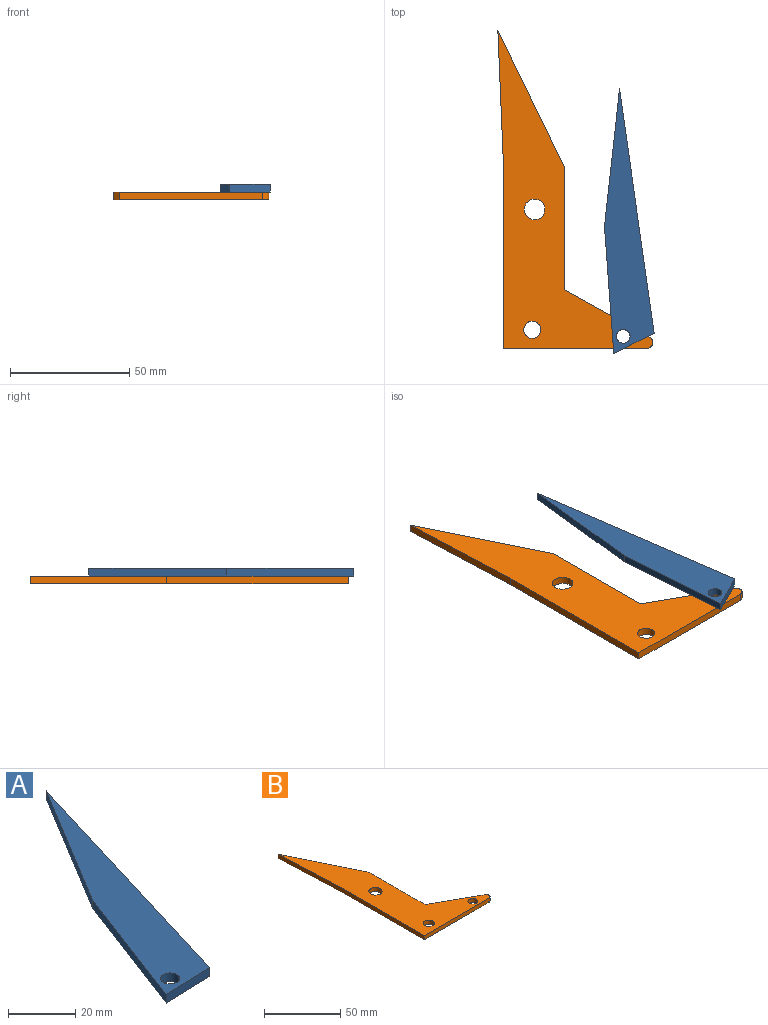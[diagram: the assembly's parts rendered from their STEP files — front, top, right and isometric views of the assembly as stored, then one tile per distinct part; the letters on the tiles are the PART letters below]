
ASSEMBLY  parts=2 mates=1
PART A: 7 faces, bbox 49.1x99.5x3.2 mm
  f0: plane 49.68x30.14mm, normal (-0.85,0.52,0), area 184.5mm2, adj f1,f3,f5,f6
  f1: plane 49.87x18.95mm, normal (-0.93,0.36,0), area 169.4mm2, adj f0,f2,f5,f6
  f2: plane 18.95x3.18mm, normal (0.03,-1,0), area 60.2mm2, adj f1,f3,f5,f6
  f3: plane 98.96x30.14mm, normal (0.96,-0.29,0), area 328.4mm2, adj f0,f2,f5,f6
  f4: cylinder r=2.86mm len=5.72mm, axis (0,0,-1), area 57mm2, adj f5,f6
  f5: plane 99.55x49.09mm, normal (0,0,1), area 1183.9mm2, adj f0,f1,f2,f3,f4
  f6: plane 99.55x49.09mm, normal (0,0,-1), area 1183.9mm2, adj f0,f1,f2,f3,f4
PART B: 12 faces, bbox 64.9x133.3x3.2 mm
  f0: plane 57.1x3.18mm, normal (-1,-0.04,0), area 181.5mm2, adj f1,f8,f10,f11
  f1: plane 76.2x3.18mm, normal (-1,0,0), area 241.9mm2, adj f0,f2,f10,f11
  f2: plane 60.01x3.18mm, normal (0,-1,0), area 190.5mm2, adj f1,f3,f10,f11
  f3: cylinder r=2.54mm len=4.76mm, axis (0,0,-1), area 21.3mm2, adj f2,f4,f10,f11
  f4: plane 35.84x19.83mm, normal (0.48,0.88,0), area 130.1mm2, adj f3,f5,f10,f11
  f5: plane 51.61x3.18mm, normal (1,0,0), area 163.9mm2, adj f4,f8,f10,f11
  f6: cylinder r=3.61mm len=7.21mm, axis (0,0,-1), area 71.9mm2, adj f10,f11
  f7: cylinder r=3.17mm len=6.35mm, axis (0,0,-1), area 63.3mm2, adj f10,f11
  f8: plane 57.1x27.78mm, normal (0.9,0.44,0), area 201.6mm2, adj f0,f5,f10,f11
  f9: cylinder r=4.33mm len=8.66mm, axis (0,0,-1), area 86.3mm2, adj f10,f11
  f10: plane 133.3x64.93mm, normal (0,0,1), area 3059.4mm2, adj f0,f1,f2,f3,f4,f5,f6,f7
  f11: plane 133.3x64.93mm, normal (0,0,-1), area 3059.4mm2, adj f0,f1,f2,f3,f4,f5,f6,f7
PLACE A rot(axis=(0,0,1),25deg) t=(32.84,-34.53,16.22)mm
PLACE B t=(8.14,-68.82,13.05)mm
MATE revolute B.f7 <-> A.f4  axis (0,0,1) through (32.92,-63.74,16.22)mm
